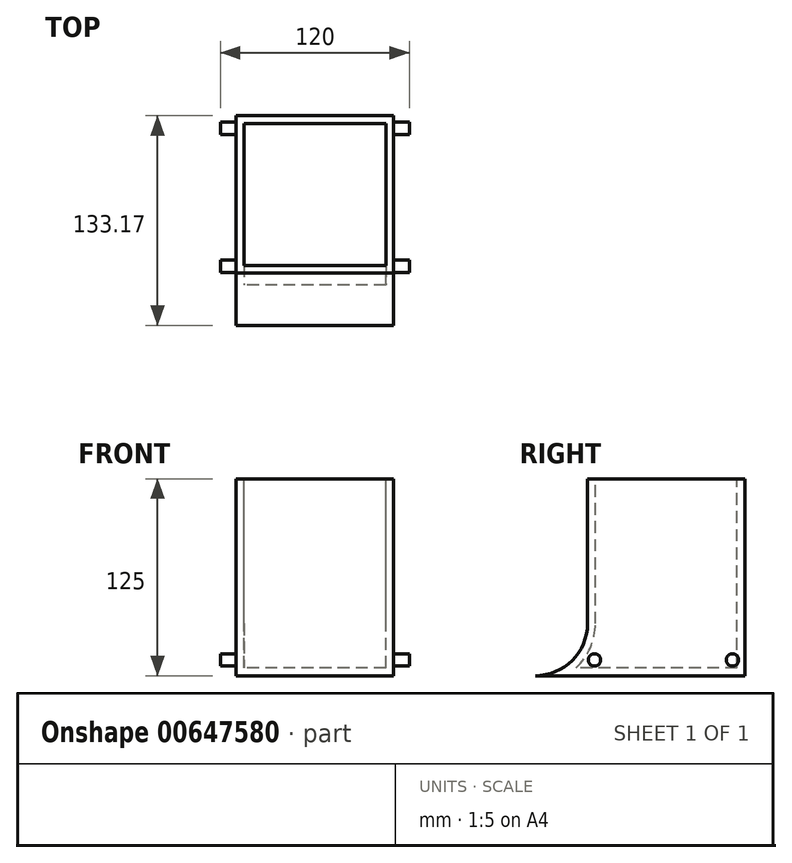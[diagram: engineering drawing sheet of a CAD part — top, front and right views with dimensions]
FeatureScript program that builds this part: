
annotation { "Feature Type Name" : "Feature", "Feature Type Description" : "" }
export const myFeature = defineFeature(function(context is Context, id is Id, definition is map)
    precondition{}
    {
        {
            var Q0;
            Q0=qCreatedBy(makeId("Right.planeOp"),FACE);
            var sketch = newSketch(context, id + "F0", { "sketchPlane" : qUnion([Q0])});
            skLineSegment(sketch, "E0.bottom", {"start": v(61.14, 0) * mm, "end": v(-38.86, 0) * mm});
            skLineSegment(sketch, "E0.top", {"start": v(61.14, 125) * mm, "end": v(-38.86, 125) * mm});
            skLineSegment(sketch, "E0.left", {"start": v(61.14, 0) * mm, "end": v(61.14, 125) * mm});
            skLineSegment(sketch, "E0.right", {"start": v(-38.86, 33.17) * mm, "end": v(-38.86, 125) * mm});
            skArc(sketch, "E1", {"start": v(-72.03, 0) * mm, "mid": v(-48.57, 9.71) * mm, "end": v(-38.86, 33.17) * mm});
            skLineSegment(sketch, "E2", {"start": v(-72.03, 0) * mm, "end": v(-38.86, 0) * mm});
            skSolve(sketch);
        }
        {
            var Q0;
            Q0=makeQuery(id+"F0.imprint","IMPRINT",FACE,{"disambiguationData":[TD([[makeQuery(id+"F0.imprint","IMPRINT",EDGE,{"derivedFrom":sQuery(id+"F0.wireOp",EDGE,"E0.bottom")}),-1.0]])]});
            extrude(context, id + "F1", {"entities" : qUnion([Q0]), "depth" : 50 * mm, "offsetDistance" : 25 * mm});
        }
        {
            var Q0;
            Q0=makeQuery(id+"F1.opExtrude","CAP_FACE",FACE,{"disambiguationData":[OSD([sQuery(id+"F0.wireOp",EDGE,"E0.bottom"),sQuery(id+"F0.wireOp",EDGE,"E0.top"),sQuery(id+"F0.wireOp",EDGE,"E0.left"),sQuery(id+"F0.wireOp",EDGE,"E0.right"),sQuery(id+"F0.wireOp",EDGE,"E1"),sQuery(id+"F0.wireOp",EDGE,"E2")])],"isStart":false});
            var sketch = newSketch(context, id + "F2", { "sketchPlane" : qUnion([Q0])});
            skCircle(sketch, "E3", {"center": v(-34.45, 10) * mm, "radius": 3.9 * mm});
            skCircle(sketch, "E4", {"center": v(53.19, 10) * mm, "radius": 3.9 * mm});
            skSolve(sketch);
        }
        {
            var Q0;
            Q0=makeQuery(id+"F2.imprint","IMPRINT",FACE,{"disambiguationData":[TD([[makeQuery(id+"F2.imprint","IMPRINT",EDGE,{"derivedFrom":sQuery(id+"F2.wireOp",EDGE,"E3")}),1.0]])]});
            var Q1;
            Q1=makeQuery(id+"F2.imprint","IMPRINT",FACE,{"disambiguationData":[TD([[makeQuery(id+"F2.imprint","IMPRINT",EDGE,{"derivedFrom":sQuery(id+"F2.wireOp",EDGE,"E4")}),1.0]])]});
            extrude(context, id + "F3", {"entities" : qUnion([Q0, Q1]), "operationType" : NewBodyOperationType.ADD, "depth" : 10 * mm, "offsetDistance" : 25 * mm});
        }
        {
            var Q0;
            Q0=makeQuery(id+"F1.opExtrude","SWEPT_BODY",BODY,{"disambiguationData":[OSD([sQuery(id+"F0.wireOp",EDGE,"E0.bottom"),sQuery(id+"F0.wireOp",EDGE,"E0.top"),sQuery(id+"F0.wireOp",EDGE,"E0.left"),sQuery(id+"F0.wireOp",EDGE,"E0.right"),sQuery(id+"F0.wireOp",EDGE,"E1"),sQuery(id+"F0.wireOp",EDGE,"E2")])]});
            var Q1;
            Q1=qCreatedBy(makeId("Right.planeOp"),FACE);
            mirror(context, id + "F4", {"operationType" : NewBodyOperationType.ADD, "entities" : qUnion([Q0]), "mirrorPlane" : qUnion([Q1])});
        }
        {
            var Q0;
            Q0=makeQuery(id+"F1.opExtrude","SWEPT_FACE",FACE,{"disambiguationData":[OSD([sQuery(id+"F0.wireOp",EDGE,"E0.top")])]});
            shell(context, id + "F5", {"entities" : qUnion([Q0]), "thickness" : 5 * mm});
        }
    });
